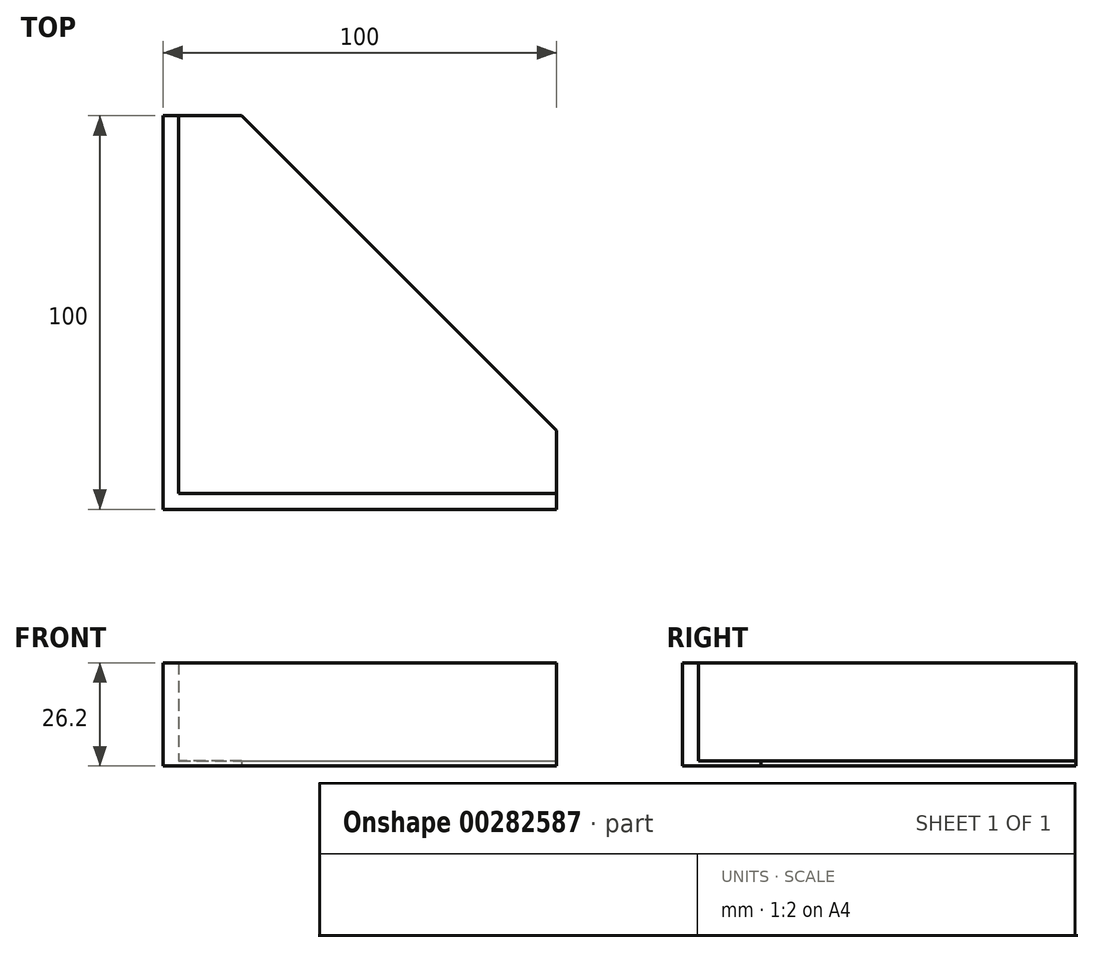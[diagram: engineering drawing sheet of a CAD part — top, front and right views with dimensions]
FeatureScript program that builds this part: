
annotation { "Feature Type Name" : "Feature", "Feature Type Description" : "" }
export const myFeature = defineFeature(function(context is Context, id is Id, definition is map)
    precondition{}
    {
        {
            var Q0;
            Q0=qCreatedBy(makeId("Top.planeOp"),FACE);
            var sketch = newSketch(context, id + "F0", { "sketchPlane" : qUnion([Q0])});
            skLineSegment(sketch, "E0.bottom", {"start": v(50, -50) * mm, "end": v(-50, -50) * mm});
            skLineSegment(sketch, "E0.top", {"start": v(-30, 50) * mm, "end": v(-50, 50) * mm});
            skLineSegment(sketch, "E0.left", {"start": v(50, -50) * mm, "end": v(50, -30) * mm});
            skLineSegment(sketch, "E0.right", {"start": v(-50, -50) * mm, "end": v(-50, 50) * mm});
            skPoint(sketch, "E0.middle", {"position": v(0, 0) * mm});
            skLineSegment(sketch, "E1", {"start": v(-30, 50) * mm, "end": v(50, -30) * mm});
            skSolve(sketch);
        }
        {
            var Q0;
            Q0=makeQuery(id+"F0.imprint","IMPRINT",FACE,{"disambiguationData":[TD([[makeQuery(id+"F0.imprint","IMPRINT",EDGE,{"derivedFrom":sQuery(id+"F0.wireOp",EDGE,"E0.bottom")}),-1.0]])]});
            extrude(context, id + "F1", {"entities" : qUnion([Q0]), "depth" : 1.2 * mm});
        }
        {
            var Q0;
            Q0=makeQuery(id+"F1.opExtrude","CAP_FACE",FACE,{"disambiguationData":[OSD([sQuery(id+"F0.wireOp",EDGE,"E0.bottom"),sQuery(id+"F0.wireOp",EDGE,"E0.top"),sQuery(id+"F0.wireOp",EDGE,"E0.left"),sQuery(id+"F0.wireOp",EDGE,"E0.right"),sQuery(id+"F0.wireOp",EDGE,"E1")])],"isStart":false});
            var sketch = newSketch(context, id + "F2", { "sketchPlane" : qUnion([Q0])});
            skLineSegment(sketch, "E2.0", {"start": v(-50, -50) * mm, "end": v(-50, 50) * mm});
            skLineSegment(sketch, "E2.1", {"start": v(50, -50) * mm, "end": v(-50, -50) * mm});
            skLineSegment(sketch, "E2.2", {"start": v(-46, 50) * mm, "end": v(-50, 50) * mm});
            skLineSegment(sketch, "E2.3", {"start": v(50, -50) * mm, "end": v(50, -46) * mm});
            skLineSegment(sketch, "E3", {"start": v(-46, 50) * mm, "end": v(-46, -46) * mm});
            skLineSegment(sketch, "E4", {"start": v(-46, -46) * mm, "end": v(50, -46) * mm});
            skPoint(sketch, "E5.orphan", {"position": v(-30, 50) * mm});
            skPoint(sketch, "E6.orphan", {"position": v(50, -30) * mm});
            skSolve(sketch);
        }
        {
            var Q0;
            Q0=makeQuery(id+"F2.imprint","IMPRINT",FACE,{"disambiguationData":[TD([[makeQuery(id+"F2.imprint","IMPRINT",EDGE,{"derivedFrom":sQuery(id+"F2.wireOp",EDGE,"E2.0")}),-1.0]])]});
            extrude(context, id + "F3", {"entities" : qUnion([Q0]), "operationType" : NewBodyOperationType.ADD, "depth" : 25 * mm});
        }
    });
